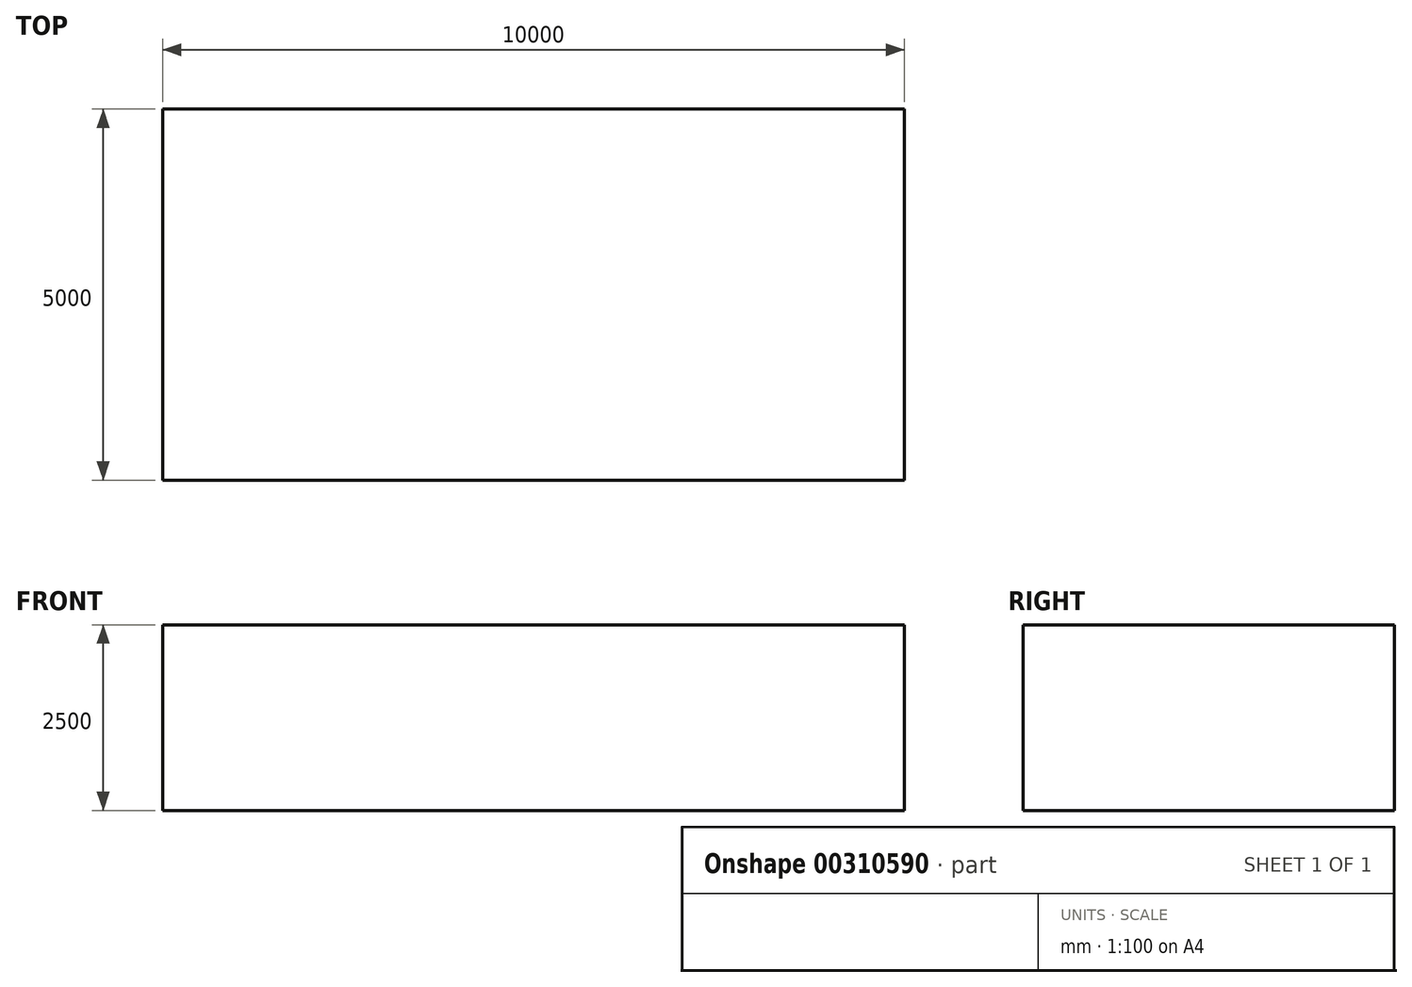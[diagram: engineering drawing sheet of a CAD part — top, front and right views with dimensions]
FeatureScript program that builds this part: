
annotation { "Feature Type Name" : "Feature", "Feature Type Description" : "" }
export const myFeature = defineFeature(function(context is Context, id is Id, definition is map)
    precondition{}
    {
        {
            var Q0;
            Q0=qCreatedBy(makeId("Front.planeOp"),FACE);
            var sketch = newSketch(context, id + "F0", { "sketchPlane" : qUnion([Q0])});
            skLineSegment(sketch, "E0", {"start": v(0, 0) * mm, "end": v(-10000, 0) * mm});
            skLineSegment(sketch, "E1", {"start": v(-10000, 0) * mm, "end": v(-10000, 2500) * mm});
            skLineSegment(sketch, "E2", {"start": v(-10000, 2500) * mm, "end": v(0, 2500) * mm});
            skLineSegment(sketch, "E3", {"start": v(0, 2500) * mm, "end": v(0, 0) * mm});
            skSolve(sketch);
        }
        {
            var Q0;
            Q0=makeQuery(id+"F0.imprint","IMPRINT",FACE,{"disambiguationData":[TD([[makeQuery(id+"F0.imprint","IMPRINT",EDGE,{"derivedFrom":sQuery(id+"F0.wireOp",EDGE,"E0")}),-1.0]])]});
            extrude(context, id + "F1", {"entities" : qUnion([Q0]), "depth" : 5000 * mm});
        }
    });
